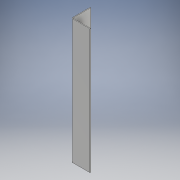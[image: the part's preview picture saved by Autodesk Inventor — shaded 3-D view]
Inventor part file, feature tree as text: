
AUTODESK INVENTOR PART (.ipt)
format: ipt  version: 2017 (Build 210142000, 142)  size: 105,984 bytes
history: native  units: mm
features: sheet_metal_op x3, sketch x1, other x1
ambient origin geometry x8: Origin, YZ Plane, XZ Plane, XY Plane, X Axis, Y Axis, Z Axis, Center Point
bodies: Solid1 (feature_tree)
feature tree (5):
  sheet_metal_op  "Contour Flange1"
  sketch  "Sketch1"  dims[d0=40.0mm d1=40.0mm d2=1.5mm d3=0.75mm d4=3.0mm d5=1.5mm d6=268.0mm d7=1.5mm d8=0.5mm d9=6.0mm d10=1.5mm d11=1.5mm]
  other  "Plate1"
  sheet_metal_op  "Bend1"
  sheet_metal_op  "Corner1"
